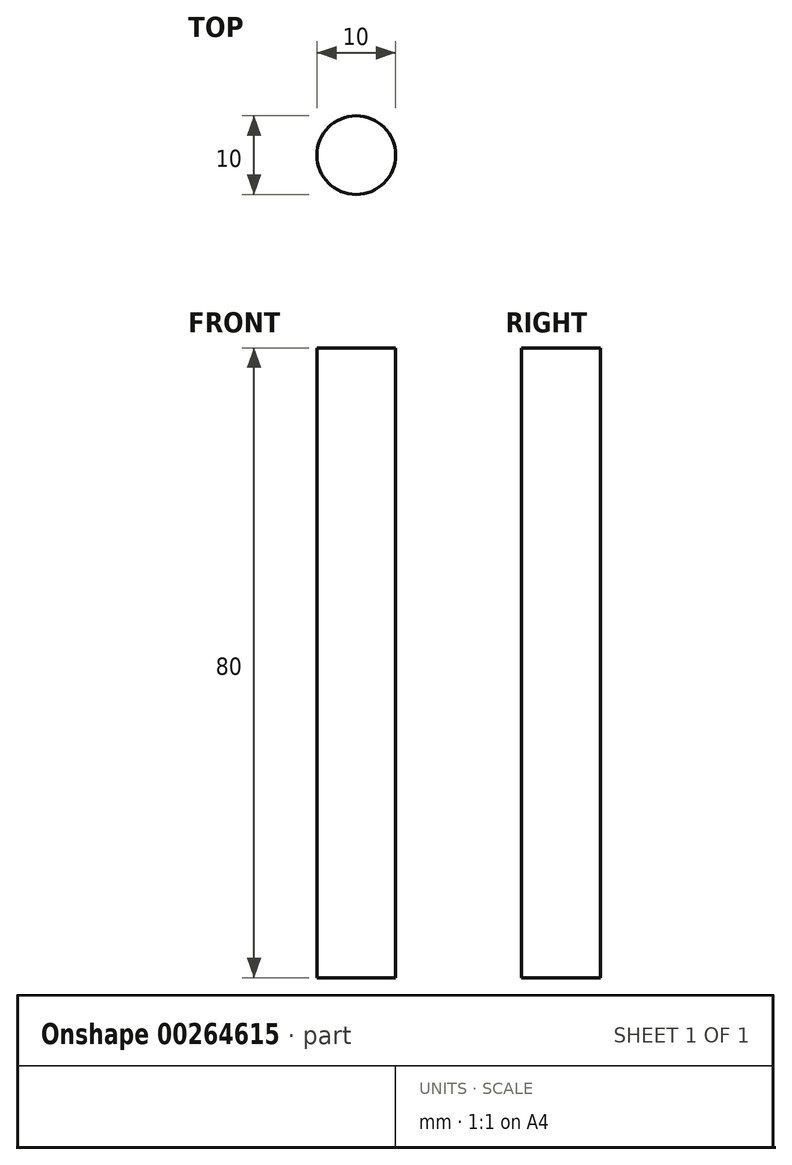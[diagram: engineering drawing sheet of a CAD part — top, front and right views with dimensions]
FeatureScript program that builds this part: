
annotation { "Feature Type Name" : "Feature", "Feature Type Description" : "" }
export const myFeature = defineFeature(function(context is Context, id is Id, definition is map)
    precondition{}
    {
        {
            var Q0;
            Q0=qCreatedBy(makeId("Top.planeOp"),FACE);
            var sketch = newSketch(context, id + "F0", { "sketchPlane" : qUnion([Q0])});
            skCircle(sketch, "E0", {"center": v(-1.67, -9.86) * mm, "radius": 5 * mm});
            skSolve(sketch);
        }
        {
            var Q0;
            Q0=makeQuery(id+"F0.imprint","IMPRINT",FACE,{"disambiguationData":[TD([[makeQuery(id+"F0.imprint","IMPRINT",EDGE,{"derivedFrom":sQuery(id+"F0.wireOp",EDGE,"E0")}),1.0]])]});
            extrude(context, id + "F1", {"entities" : qUnion([Q0]), "depth" : 80 * mm});
        }
    });
